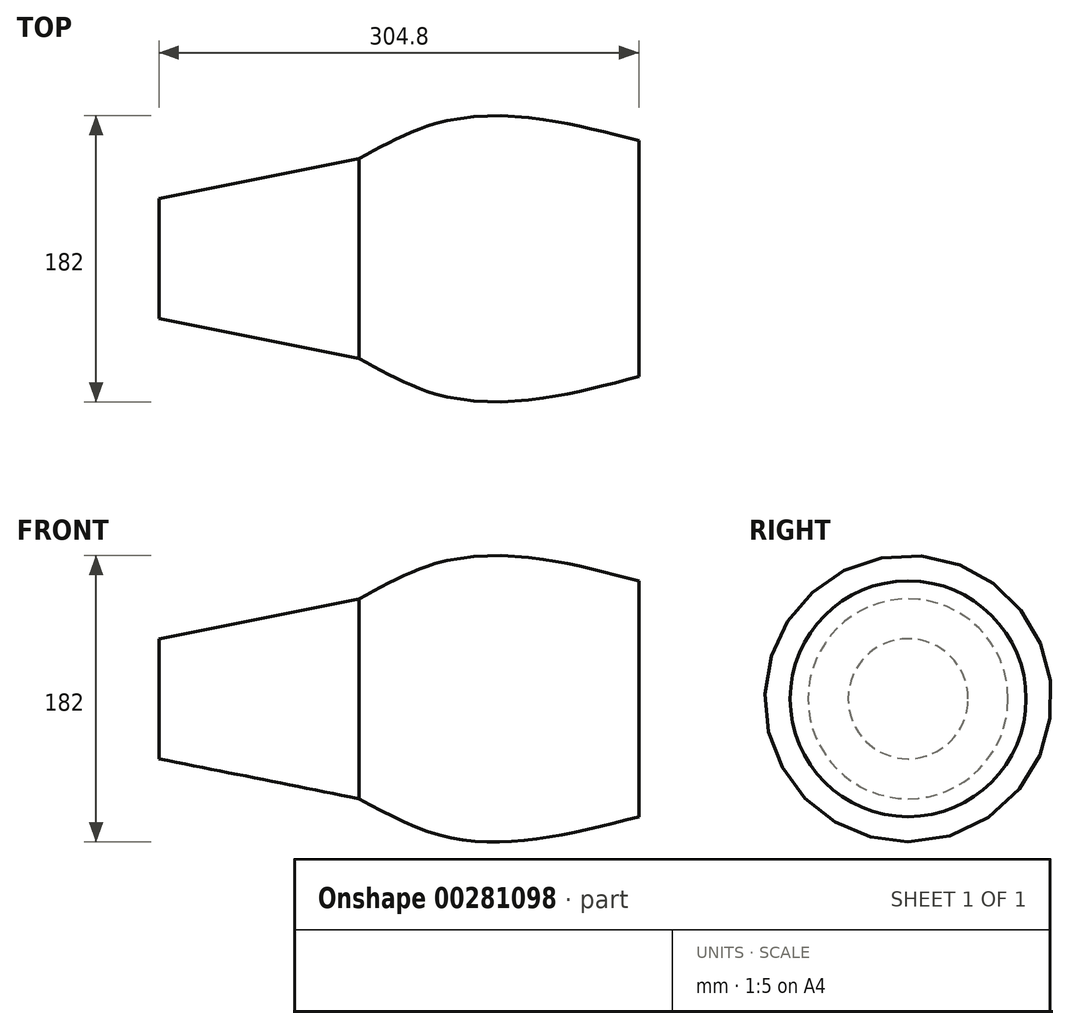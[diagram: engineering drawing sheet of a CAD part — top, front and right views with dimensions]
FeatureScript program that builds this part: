
annotation { "Feature Type Name" : "Feature", "Feature Type Description" : "" }
export const myFeature = defineFeature(function(context is Context, id is Id, definition is map)
    precondition{}
    {
        {
            var Q0;
            Q0=qCreatedBy(makeId("Right.planeOp"),FACE);
            cPlane(context, id + "F0", {"entities" : qUnion([Q0]), "cplaneType" : CPlaneType.OFFSET, "offset" : 127 * mm, "oppositeDirection" : true, "width" : 152.4 * mm, "height" : 152.4 * mm});
        }
        {
            var Q0;
            Q0=qCreatedBy(makeId("Right.planeOp"),FACE);
            var sketch = newSketch(context, id + "F1", { "sketchPlane" : qUnion([Q0])});
            skCircle(sketch, "E0", {"center": v(0, 0) * mm, "radius": 63.5 * mm});
            skSolve(sketch);
        }
        {
            var Q0;
            Q0=qCreatedBy(id+"F0.planeOp",FACE);
            var sketch = newSketch(context, id + "F2", { "sketchPlane" : qUnion([Q0])});
            skCircle(sketch, "E1", {"center": v(0, 0) * mm, "radius": 38.1 * mm});
            skSolve(sketch);
        }
        {
            var Q0;
            Q0=makeQuery(id+"F2.imprint","IMPRINT",FACE,{"disambiguationData":[TD([[makeQuery(id+"F2.imprint","IMPRINT",EDGE,{"derivedFrom":sQuery(id+"F2.wireOp",EDGE,"E1")}),1.0]])]});
            var Q1;
            Q1=makeQuery(id+"F1.imprint","IMPRINT",FACE,{"disambiguationData":[TD([[makeQuery(id+"F1.imprint","IMPRINT",EDGE,{"derivedFrom":sQuery(id+"F1.wireOp",EDGE,"E0")}),1.0]])]});
            loft(context, id + "F3", {"sheetProfilesArray" : [{ "sheetProfileEntities" : qUnion([Q0]) }, { "sheetProfileEntities" : qUnion([Q1]) }]});
        }
        {
            var Q0;
            Q0=qCreatedBy(makeId("Right.planeOp"),FACE);
            cPlane(context, id + "F4", {"entities" : qUnion([Q0]), "cplaneType" : CPlaneType.OFFSET, "offset" : 50.8 * mm, "width" : 152.4 * mm, "height" : 152.4 * mm});
        }
        {
            var Q0;
            Q0=qCreatedBy(id+"F4.planeOp",FACE);
            cPlane(context, id + "F5", {"entities" : qUnion([Q0]), "cplaneType" : CPlaneType.OFFSET, "offset" : 127 * mm, "width" : 152.4 * mm, "height" : 152.4 * mm});
        }
        {
            var Q0;
            Q0=qCreatedBy(id+"F4.planeOp",FACE);
            var sketch = newSketch(context, id + "F6", { "sketchPlane" : qUnion([Q0])});
            skCircle(sketch, "E2", {"center": v(0, 0) * mm, "radius": 86.5 * mm});
            skSolve(sketch);
        }
        {
            var Q0;
            Q0=qCreatedBy(id+"F5.planeOp",FACE);
            var sketch = newSketch(context, id + "F7", { "sketchPlane" : qUnion([Q0])});
            skCircle(sketch, "E3", {"center": v(0, 0) * mm, "radius": 74.92 * mm});
            skSolve(sketch);
        }
        {
            var Q0;
            Q0=makeQuery(id+"F3.opLoft","CAP_FACE",FACE,{"disambiguationData":[OSD([makeQuery(id+"F1.imprint","IMPRINT",FACE,{"disambiguationData":[TD([[makeQuery(id+"F1.imprint","IMPRINT",EDGE,{"derivedFrom":sQuery(id+"F1.wireOp",EDGE,"E0")}),1.0]])]})])],"isStart":true});
            var Q1;
            Q1=makeQuery(id+"F6.imprint","IMPRINT",FACE,{"disambiguationData":[TD([[makeQuery(id+"F6.imprint","IMPRINT",EDGE,{"derivedFrom":sQuery(id+"F6.wireOp",EDGE,"E2")}),1.0]])]});
            var Q2;
            Q2=makeQuery(id+"F7.imprint","IMPRINT",FACE,{"disambiguationData":[TD([[makeQuery(id+"F7.imprint","IMPRINT",EDGE,{"derivedFrom":sQuery(id+"F7.wireOp",EDGE,"E3")}),1.0]])]});
            loft(context, id + "F8", {"sheetProfilesArray" : [{ "sheetProfileEntities" : qUnion([Q0]) }, { "sheetProfileEntities" : qUnion([Q1]) }, { "sheetProfileEntities" : qUnion([Q2]) }]});
        }
    });
